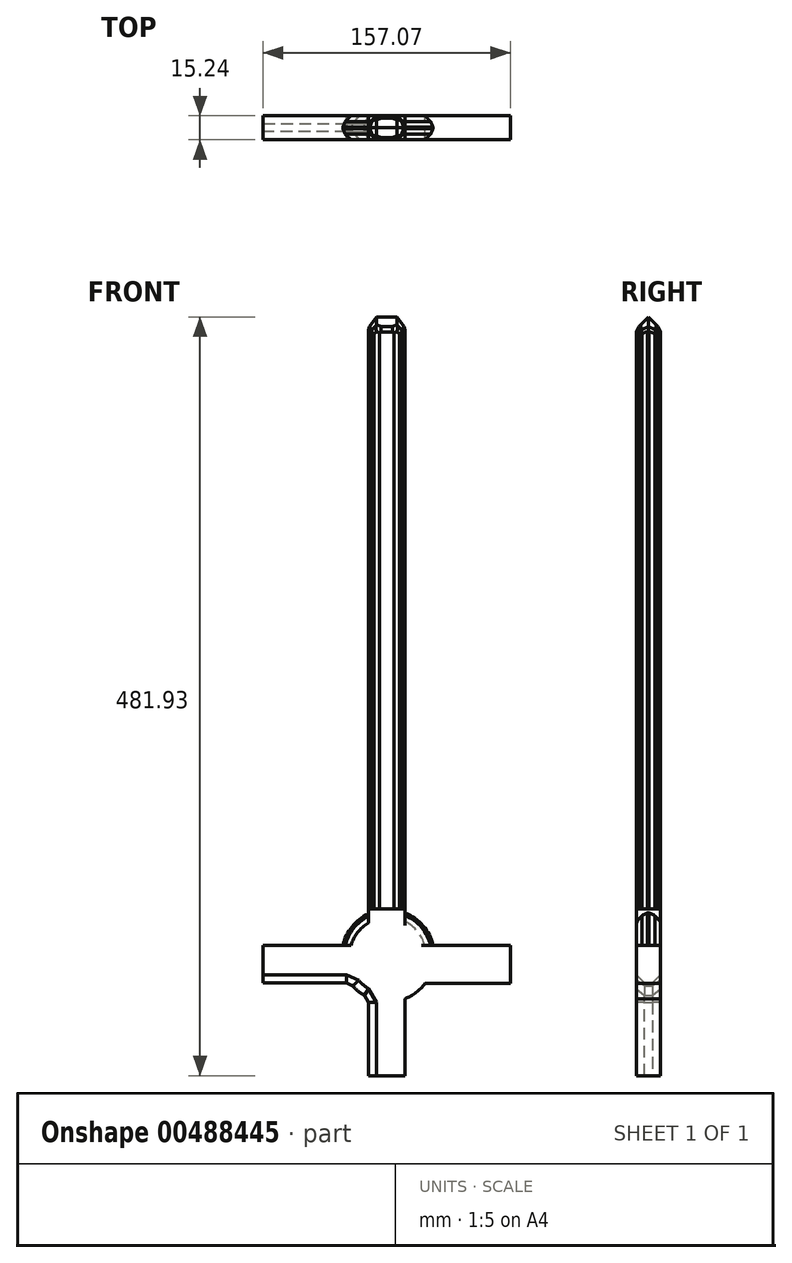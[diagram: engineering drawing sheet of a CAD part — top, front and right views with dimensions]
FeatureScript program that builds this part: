
annotation { "Feature Type Name" : "Feature", "Feature Type Description" : "" }
export const myFeature = defineFeature(function(context is Context, id is Id, definition is map)
    precondition{}
    {
        {
            var Q0;
            Q0=qCreatedBy(makeId("Front.planeOp"),FACE);
            var sketch = newSketch(context, id + "F0", { "sketchPlane" : qUnion([Q0])});
            skLineSegment(sketch, "E0.bottom", {"start": v(10.92, 47.62) * mm, "end": v(-12.46, 47.62) * mm});
            skLineSegment(sketch, "E0.top", {"start": v(10.92, 24.24) * mm, "end": v(-12.46, 24.24) * mm});
            skLineSegment(sketch, "E0.left", {"start": v(10.92, 47.62) * mm, "end": v(10.92, 24.24) * mm});
            skLineSegment(sketch, "E0.right", {"start": v(-12.46, 47.62) * mm, "end": v(-12.46, 24.24) * mm});
            skLineSegment(sketch, "E1.bottom", {"start": v(-12.46, 24.24) * mm, "end": v(-41.2, 24.24) * mm});
            skLineSegment(sketch, "E1.top", {"start": v(-12.46, 0.48) * mm, "end": v(-41.2, 0.48) * mm});
            skLineSegment(sketch, "E1.left", {"start": v(-12.46, 24.24) * mm, "end": v(-12.46, 0.48) * mm});
            skLineSegment(sketch, "E1.right", {"start": v(-41.2, 24.24) * mm, "end": v(-41.2, 0.48) * mm});
            skLineSegment(sketch, "E2.bottom", {"start": v(-12.46, 24.24) * mm, "end": v(10.92, 24.24) * mm});
            skLineSegment(sketch, "E2.top", {"start": v(-12.46, 0.29) * mm, "end": v(10.92, 0.29) * mm});
            skLineSegment(sketch, "E2.left", {"start": v(-12.46, 24.24) * mm, "end": v(-12.46, 0.29) * mm});
            skLineSegment(sketch, "E2.right", {"start": v(10.92, 24.24) * mm, "end": v(10.92, 0.29) * mm});
            skLineSegment(sketch, "E3.bottom", {"start": v(10.92, 24.24) * mm, "end": v(39.67, 24.24) * mm});
            skLineSegment(sketch, "E3.top", {"start": v(10.92, 0.1) * mm, "end": v(39.67, 0.1) * mm});
            skLineSegment(sketch, "E3.left", {"start": v(10.92, 24.24) * mm, "end": v(10.92, 0.1) * mm});
            skLineSegment(sketch, "E3.right", {"start": v(39.67, 24.24) * mm, "end": v(39.67, 0.1) * mm});
            skSolve(sketch);
        }
        {
            var Q0;
            Q0 = qSketchRegion(id + "F0", true);
            extrude(context, id + "F1", {"entities" : qUnion([Q0]), "depth" : 15.24 * mm});
        }
        {
            var Q0;
            Q0=makeQuery(id+"F1.opExtrude","SWEPT_FACE",FACE,{"disambiguationData":[OSD([sQuery(id+"F0.wireOp",EDGE,"E2.top")])]});
            extrude(context, id + "F2", {"entities" : qUnion([Q0]), "operationType" : NewBodyOperationType.ADD, "depth" : 58.67 * mm});
        }
        {
            var Q0;
            Q0=makeQuery(id+"F1.opExtrude","SWEPT_FACE",FACE,{"disambiguationData":[OSD([sQuery(id+"F0.wireOp",EDGE,"E0.bottom")])]});
            extrude(context, id + "F3", {"entities" : qUnion([Q0]), "depth" : 381 * mm});
        }
        {
            var Q0;
            Q0=makeQuery(id+"F1.opExtrude","SWEPT_FACE",FACE,{"disambiguationData":[OSD([sQuery(id+"F0.wireOp",EDGE,"E1.right")])]});
            extrude(context, id + "F4", {"entities" : qUnion([Q0]), "operationType" : NewBodyOperationType.ADD, "depth" : 38.1 * mm});
        }
        {
            var Q0;
            Q0=makeQuery(id+"F1.opExtrude","SWEPT_FACE",FACE,{"disambiguationData":[OSD([sQuery(id+"F0.wireOp",EDGE,"E3.right")])]});
            extrude(context, id + "F5", {"entities" : qUnion([Q0]), "operationType" : NewBodyOperationType.ADD, "depth" : 38.1 * mm});
        }
        {
            var Q0;
            {var subQ0=sQuery(id+"F0.wireOp",EDGE,"E0.bottom");Q0=makeQuery(id+"F3.opExtrude","CAP_EDGE",EDGE,{"disambiguationData":[OSD([subQ0]),TDD([makeQuery(id+"F1.opExtrude","CAP_EDGE",EDGE,{"disambiguationData":[OSD([subQ0])],"isStart":true})])],"isStart":false});}
            var Q1;
            {var subQ0=sQuery(id+"F0.wireOp",EDGE,"E0.bottom");Q1=makeQuery(id+"F3.opExtrude","CAP_EDGE",EDGE,{"disambiguationData":[OSD([subQ0]),TDD([makeQuery(id+"F1.opExtrude","CAP_EDGE",EDGE,{"disambiguationData":[OSD([subQ0])],"isStart":false})])],"isStart":false});}
            chamfer(context, id + "F6", {"entities" : qUnion([Q0, Q1]), "width" : 12.7 * mm, "tangentPropagation" : true});
        }
        {
            var Q0;
            {var subQ0=sQuery(id+"F0.wireOp",EDGE,"E0.bottom");Q0=makeQuery(id+"F6.opChamfer","BLEND_EDGE",EDGE,{"blendedFrom":[makeQuery(id+"F3.opExtrude","CAP_EDGE",EDGE,{"disambiguationData":[OSD([subQ0]),TDD([makeQuery(id+"F1.opExtrude","CAP_EDGE",EDGE,{"disambiguationData":[OSD([subQ0])],"isStart":true})])],"isStart":false}),makeQuery(id+"F3.opExtrude","SWEPT_FACE",FACE,{"disambiguationData":[OSD([subQ0,sQuery(id+"F0.wireOp",EDGE,"E0.left")])]})],"blendedInto":[makeQuery(id+"F3.opExtrude","SWEPT_FACE",FACE,{"disambiguationData":[OSD([subQ0,sQuery(id+"F0.wireOp",EDGE,"E0.left")])]})]});}
            var Q1;
            {var subQ0=sQuery(id+"F0.wireOp",EDGE,"E0.bottom");Q1=makeQuery(id+"F6.opChamfer","BLEND_EDGE",EDGE,{"blendedFrom":[makeQuery(id+"F3.opExtrude","CAP_EDGE",EDGE,{"disambiguationData":[OSD([subQ0]),TDD([makeQuery(id+"F1.opExtrude","CAP_EDGE",EDGE,{"disambiguationData":[OSD([subQ0])],"isStart":false})])],"isStart":false}),makeQuery(id+"F3.opExtrude","SWEPT_FACE",FACE,{"disambiguationData":[OSD([subQ0,sQuery(id+"F0.wireOp",EDGE,"E0.left")])]})],"blendedInto":[makeQuery(id+"F3.opExtrude","SWEPT_FACE",FACE,{"disambiguationData":[OSD([subQ0,sQuery(id+"F0.wireOp",EDGE,"E0.left")])]})]});}
            var Q2;
            {var subQ0=sQuery(id+"F0.wireOp",EDGE,"E0.bottom");Q2=makeQuery(id+"F6.opChamfer","BLEND_EDGE",EDGE,{"blendedFrom":[makeQuery(id+"F3.opExtrude","CAP_EDGE",EDGE,{"disambiguationData":[OSD([subQ0]),TDD([makeQuery(id+"F1.opExtrude","CAP_EDGE",EDGE,{"disambiguationData":[OSD([subQ0])],"isStart":false})])],"isStart":false}),makeQuery(id+"F3.opExtrude","SWEPT_FACE",FACE,{"disambiguationData":[OSD([subQ0,sQuery(id+"F0.wireOp",EDGE,"E0.right")])]})],"blendedInto":[makeQuery(id+"F3.opExtrude","SWEPT_FACE",FACE,{"disambiguationData":[OSD([subQ0,sQuery(id+"F0.wireOp",EDGE,"E0.right")])]})]});}
            var Q3;
            {var subQ0=sQuery(id+"F0.wireOp",EDGE,"E0.bottom");Q3=makeQuery(id+"F6.opChamfer","BLEND_EDGE",EDGE,{"blendedFrom":[makeQuery(id+"F3.opExtrude","CAP_EDGE",EDGE,{"disambiguationData":[OSD([subQ0]),TDD([makeQuery(id+"F1.opExtrude","CAP_EDGE",EDGE,{"disambiguationData":[OSD([subQ0])],"isStart":true})])],"isStart":false}),makeQuery(id+"F3.opExtrude","SWEPT_FACE",FACE,{"disambiguationData":[OSD([subQ0,sQuery(id+"F0.wireOp",EDGE,"E0.right")])]})],"blendedInto":[makeQuery(id+"F3.opExtrude","SWEPT_FACE",FACE,{"disambiguationData":[OSD([subQ0,sQuery(id+"F0.wireOp",EDGE,"E0.right")])]})]});}
            chamfer(context, id + "F7", {"entities" : qUnion([Q0, Q1, Q2, Q3]), "width" : 5.08 * mm, "tangentPropagation" : true});
        }
        {
            var Q0;
            {var subQ0=sQuery(id+"F0.wireOp",EDGE,"E0.right");var subQ1=sQuery(id+"F0.wireOp",EDGE,"E0.bottom");Q0=makeQuery(id+"F3.opExtrude","SWEPT_EDGE",EDGE,{"disambiguationData":[OSD([subQ1,subQ0]),TDD([makeQuery(id+"F1.opExtrude","CAP_VERTEX",VERTEX,{"disambiguationData":[OSD([subQ1,subQ0])],"isStart":false})])]});}
            var Q1;
            {var subQ0=sQuery(id+"F0.wireOp",EDGE,"E0.left");var subQ1=sQuery(id+"F0.wireOp",EDGE,"E0.bottom");Q1=makeQuery(id+"F3.opExtrude","SWEPT_EDGE",EDGE,{"disambiguationData":[OSD([subQ1,subQ0]),TDD([makeQuery(id+"F1.opExtrude","CAP_VERTEX",VERTEX,{"disambiguationData":[OSD([subQ1,subQ0])],"isStart":false})])]});}
            var Q2;
            {var subQ0=sQuery(id+"F0.wireOp",EDGE,"E0.left");var subQ1=sQuery(id+"F0.wireOp",EDGE,"E0.bottom");Q2=makeQuery(id+"F3.opExtrude","SWEPT_EDGE",EDGE,{"disambiguationData":[OSD([subQ1,subQ0]),TDD([makeQuery(id+"F1.opExtrude","CAP_VERTEX",VERTEX,{"disambiguationData":[OSD([subQ1,subQ0])],"isStart":true})])]});}
            var Q3;
            {var subQ0=sQuery(id+"F0.wireOp",EDGE,"E0.right");var subQ1=sQuery(id+"F0.wireOp",EDGE,"E0.bottom");Q3=makeQuery(id+"F3.opExtrude","SWEPT_EDGE",EDGE,{"disambiguationData":[OSD([subQ1,subQ0]),TDD([makeQuery(id+"F1.opExtrude","CAP_VERTEX",VERTEX,{"disambiguationData":[OSD([subQ1,subQ0])],"isStart":true})])]});}
            chamfer(context, id + "F8", {"entities" : qUnion([Q0, Q1, Q2, Q3]), "width" : 5.08 * mm, "tangentPropagation" : true});
        }
        {
            var Q0;
            Q0=qCreatedBy(makeId("Front.planeOp"),FACE);
            var sketch = newSketch(context, id + "F9", { "sketchPlane" : qUnion([Q0])});
            skCircle(sketch, "E4", {"center": v(0, 17.76) * mm, "radius": 29.39 * mm});
            skSolve(sketch);
        }
        {
            var Q0;
            Q0 = qSketchRegion(id + "F9", true);
            extrude(context, id + "F10", {"entities" : qUnion([Q0]), "operationType" : NewBodyOperationType.ADD, "depth" : 15.24 * mm});
        }
        {
            var Q0;
            {var subQ4=sQuery(id+"F0.wireOp",EDGE,"E0.right");var subQ5=sQuery(id+"F9.wireOp",EDGE,"E4");Q0=makeQuery(id+"F10.boolean.opBoolean","SPLIT",EDGE,{"disambiguationData":[TD([makeQuery(id+"F1.opExtrude","SWEPT_FACE",FACE,{"disambiguationData":[OSD([subQ4])]})])],"derivedFrom":makeQuery(id+"F10.opExtrude","CAP_EDGE",EDGE,{"disambiguationData":[OSD([subQ5])],"isStart":false})});}
            var Q1;
            {var subQ3=sQuery(id+"F0.wireOp",EDGE,"E0.right");var subQ5=sQuery(id+"F9.wireOp",EDGE,"E4");Q1=makeQuery(id+"F10.boolean.opBoolean","SPLIT",EDGE,{"disambiguationData":[TD([makeQuery(id+"F1.opExtrude","SWEPT_FACE",FACE,{"disambiguationData":[OSD([subQ3])]})])],"derivedFrom":makeQuery(id+"F10.opExtrude","CAP_EDGE",EDGE,{"disambiguationData":[OSD([subQ5])],"isStart":true})});}
            var Q2;
            {var subQ2=sQuery(id+"F0.wireOp",EDGE,"E0.left");var subQ5=sQuery(id+"F9.wireOp",EDGE,"E4");Q2=makeQuery(id+"F10.boolean.opBoolean","SPLIT",EDGE,{"disambiguationData":[TD([makeQuery(id+"F1.opExtrude","SWEPT_FACE",FACE,{"disambiguationData":[OSD([subQ2])]})])],"derivedFrom":makeQuery(id+"F10.opExtrude","CAP_EDGE",EDGE,{"disambiguationData":[OSD([subQ5])],"isStart":true})});}
            var Q3;
            {var subQ2=sQuery(id+"F9.wireOp",EDGE,"E4");var subQ3=sQuery(id+"F0.wireOp",EDGE,"E0.left");Q3=makeQuery(id+"F10.boolean.opBoolean","SPLIT",EDGE,{"disambiguationData":[TD([makeQuery(id+"F1.opExtrude","SWEPT_FACE",FACE,{"disambiguationData":[OSD([subQ3])]})])],"derivedFrom":makeQuery(id+"F10.opExtrude","CAP_EDGE",EDGE,{"disambiguationData":[OSD([subQ2])],"isStart":false})});}
            chamfer(context, id + "F11", {"entities" : qUnion([Q0, Q1, Q2, Q3]), "width" : 5.08 * mm, "tangentPropagation" : true});
        }
        {
            var Q0;
            {var subQ12=sQuery(id+"F0.wireOp",EDGE,"E0.right");var subQ16=makeQuery(id+"F1.opExtrude","SWEPT_FACE",FACE,{"disambiguationData":[OSD([subQ12])]});var subQ17=sQuery(id+"F9.wireOp",EDGE,"E4");var subQ21=makeQuery(id+"F10.opExtrude","SWEPT_FACE",FACE,{"disambiguationData":[OSD([subQ17])]});Q0=makeQuery(id+"F11.opChamfer","BLEND_EDGE",EDGE,{"blendedFrom":[makeQuery(id+"F10.boolean.opBoolean","SPLIT",EDGE,{"disambiguationData":[TD([subQ16])],"derivedFrom":makeQuery(id+"F10.opExtrude","CAP_EDGE",EDGE,{"disambiguationData":[OSD([subQ17])],"isStart":false})}),makeQuery(id+"F10.boolean.opBoolean","SPLIT",FACE,{"disambiguationData":[TD([subQ16])],"derivedFrom":subQ21})],"blendedInto":[makeQuery(id+"F10.boolean.opBoolean","SPLIT",FACE,{"disambiguationData":[TD([subQ16])],"derivedFrom":subQ21})]});}
            var Q1;
            {var subQ11=sQuery(id+"F0.wireOp",EDGE,"E0.right");var subQ16=makeQuery(id+"F1.opExtrude","SWEPT_FACE",FACE,{"disambiguationData":[OSD([subQ11])]});var subQ17=sQuery(id+"F9.wireOp",EDGE,"E4");var subQ21=makeQuery(id+"F10.opExtrude","SWEPT_FACE",FACE,{"disambiguationData":[OSD([subQ17])]});Q1=makeQuery(id+"F11.opChamfer","BLEND_EDGE",EDGE,{"blendedFrom":[makeQuery(id+"F10.boolean.opBoolean","SPLIT",EDGE,{"disambiguationData":[TD([subQ16])],"derivedFrom":makeQuery(id+"F10.opExtrude","CAP_EDGE",EDGE,{"disambiguationData":[OSD([subQ17])],"isStart":true})}),makeQuery(id+"F10.boolean.opBoolean","SPLIT",FACE,{"disambiguationData":[TD([subQ16])],"derivedFrom":subQ21})],"blendedInto":[makeQuery(id+"F10.boolean.opBoolean","SPLIT",FACE,{"disambiguationData":[TD([subQ16])],"derivedFrom":subQ21})]});}
            var Q2;
            {var subQ14=sQuery(id+"F0.wireOp",EDGE,"E0.left");var subQ18=makeQuery(id+"F1.opExtrude","SWEPT_FACE",FACE,{"disambiguationData":[OSD([subQ14])]});var subQ19=sQuery(id+"F9.wireOp",EDGE,"E4");var subQ21=makeQuery(id+"F10.opExtrude","SWEPT_FACE",FACE,{"disambiguationData":[OSD([subQ19])]});Q2=makeQuery(id+"F11.opChamfer","BLEND_EDGE",EDGE,{"blendedFrom":[makeQuery(id+"F10.boolean.opBoolean","SPLIT",EDGE,{"disambiguationData":[TD([subQ18])],"derivedFrom":makeQuery(id+"F10.opExtrude","CAP_EDGE",EDGE,{"disambiguationData":[OSD([subQ19])],"isStart":false})}),makeQuery(id+"F10.boolean.opBoolean","SPLIT",FACE,{"disambiguationData":[TD([subQ18])],"derivedFrom":subQ21})],"blendedInto":[makeQuery(id+"F10.boolean.opBoolean","SPLIT",FACE,{"disambiguationData":[TD([subQ18])],"derivedFrom":subQ21})]});}
            var Q3;
            {var subQ14=sQuery(id+"F0.wireOp",EDGE,"E0.left");var subQ18=makeQuery(id+"F1.opExtrude","SWEPT_FACE",FACE,{"disambiguationData":[OSD([subQ14])]});var subQ19=sQuery(id+"F9.wireOp",EDGE,"E4");var subQ21=makeQuery(id+"F10.opExtrude","SWEPT_FACE",FACE,{"disambiguationData":[OSD([subQ19])]});Q3=makeQuery(id+"F11.opChamfer","BLEND_EDGE",EDGE,{"blendedFrom":[makeQuery(id+"F10.boolean.opBoolean","SPLIT",EDGE,{"disambiguationData":[TD([subQ18])],"derivedFrom":makeQuery(id+"F10.opExtrude","CAP_EDGE",EDGE,{"disambiguationData":[OSD([subQ19])],"isStart":true})}),makeQuery(id+"F10.boolean.opBoolean","SPLIT",FACE,{"disambiguationData":[TD([subQ18])],"derivedFrom":subQ21})],"blendedInto":[makeQuery(id+"F10.boolean.opBoolean","SPLIT",FACE,{"disambiguationData":[TD([subQ18])],"derivedFrom":subQ21})]});}
            chamfer(context, id + "F12", {"entities" : qUnion([Q0, Q1, Q2, Q3]), "width" : 5.08 * mm, "tangentPropagation" : true});
        }
        {
            var Q0;
            {var subQ0=sQuery(id+"F9.wireOp",EDGE,"E4");var subQ1=makeQuery(id+"F10.opExtrude","CAP_FACE",FACE,{"disambiguationData":[OSD([subQ0])],"isStart":false});var subQ2=sQuery(id+"F0.wireOp",EDGE,"E3.right");var subQ3=makeQuery(id+"F5.opExtrude","SWEPT_FACE",FACE,{"disambiguationData":[OSD([subQ2]),TDD([makeQuery(id+"F1.opExtrude","CAP_EDGE",EDGE,{"disambiguationData":[OSD([subQ2])],"isStart":false})])]});var subQ4=sQuery(id+"F0.wireOp",EDGE,"E1.right");var subQ5=makeQuery(id+"F4.opExtrude","SWEPT_FACE",FACE,{"disambiguationData":[OSD([subQ4]),TDD([makeQuery(id+"F1.opExtrude","CAP_EDGE",EDGE,{"disambiguationData":[OSD([subQ4])],"isStart":false})])]});var subQ6=sQuery(id+"F0.wireOp",EDGE,"E2.top");var subQ7=makeQuery(id+"F2.opExtrude","SWEPT_FACE",FACE,{"disambiguationData":[OSD([subQ6]),TDD([makeQuery(id+"F1.opExtrude","CAP_EDGE",EDGE,{"disambiguationData":[OSD([subQ6])],"isStart":false})])]});var subQ8=sQuery(id+"F0.wireOp",EDGE,"E3.bottom");var subQ9=sQuery(id+"F0.wireOp",EDGE,"E0.left");var subQ10=makeQuery(id+"F1.opExtrude","CAP_FACE",FACE,{"disambiguationData":[OSD([sQuery(id+"F0.wireOp",EDGE,"E0.bottom"),subQ9,sQuery(id+"F0.wireOp",EDGE,"E0.right"),sQuery(id+"F0.wireOp",EDGE,"E1.bottom"),sQuery(id+"F0.wireOp",EDGE,"E1.top"),subQ4,subQ6,sQuery(id+"F0.wireOp",EDGE,"E2.left"),subQ8,sQuery(id+"F0.wireOp",EDGE,"E3.top"),sQuery(id+"F0.wireOp",EDGE,"E3.left"),subQ2])],"isStart":false});Q0=makeQuery(id+"F11.opChamfer","BLEND_EDGE",EDGE,{"blendedFrom":[makeQuery(id+"F10.boolean.opBoolean","SPLIT",EDGE,{"disambiguationData":[TD([makeQuery(id+"F1.opExtrude","SWEPT_FACE",FACE,{"disambiguationData":[OSD([subQ9])]})])],"derivedFrom":makeQuery(id+"F10.opExtrude","CAP_EDGE",EDGE,{"disambiguationData":[OSD([subQ0])],"isStart":false})}),makeQuery(id+"F10.boolean.opBoolean","MERGE",FACE,{"derivedFrom":[makeQuery(id+"F5.boolean.opBoolean","MERGE",FACE,{"derivedFrom":[makeQuery(id+"F4.boolean.opBoolean","MERGE",FACE,{"derivedFrom":[makeQuery(id+"F2.boolean.opBoolean","MERGE",FACE,{"derivedFrom":[subQ10,subQ7]}),subQ5]}),subQ3]}),subQ1]})],"blendedInto":[makeQuery(id+"F10.boolean.opBoolean","MERGE",FACE,{"derivedFrom":[makeQuery(id+"F5.boolean.opBoolean","MERGE",FACE,{"derivedFrom":[makeQuery(id+"F4.boolean.opBoolean","MERGE",FACE,{"derivedFrom":[makeQuery(id+"F2.boolean.opBoolean","MERGE",FACE,{"derivedFrom":[subQ10,subQ7]}),subQ5]}),subQ3]}),subQ1]})]});}
            fillet(context, id + "F13", {"entities" : qUnion([Q0]), "radius" : 5.08 * mm, "tangentPropagation" : true, "allowEdgeOverflow" : false});
        }
        {
            var Q0;
            {var subQ0=sQuery(id+"F0.wireOp",EDGE,"E0.right");var subQ1=sQuery(id+"F0.wireOp",EDGE,"E0.bottom");Q0=makeQuery(id+"F8.opChamfer","BLEND_EDGE",EDGE,{"blendedFrom":[makeQuery(id+"F3.opExtrude","SWEPT_EDGE",EDGE,{"disambiguationData":[OSD([subQ1,subQ0]),TDD([makeQuery(id+"F1.opExtrude","CAP_VERTEX",VERTEX,{"disambiguationData":[OSD([subQ1,subQ0])],"isStart":true})])]}),makeQuery(id+"F3.opExtrude","SWEPT_FACE",FACE,{"disambiguationData":[OSD([subQ1,subQ0])]})],"blendedInto":[makeQuery(id+"F3.opExtrude","SWEPT_FACE",FACE,{"disambiguationData":[OSD([subQ1,subQ0])]})]});}
            var Q1;
            {var subQ0=sQuery(id+"F0.wireOp",EDGE,"E0.right");var subQ1=sQuery(id+"F0.wireOp",EDGE,"E0.bottom");Q1=makeQuery(id+"F8.opChamfer","BLEND_EDGE",EDGE,{"blendedFrom":[makeQuery(id+"F3.opExtrude","SWEPT_EDGE",EDGE,{"disambiguationData":[OSD([subQ1,subQ0]),TDD([makeQuery(id+"F1.opExtrude","CAP_VERTEX",VERTEX,{"disambiguationData":[OSD([subQ1,subQ0])],"isStart":false})])]}),makeQuery(id+"F3.opExtrude","SWEPT_FACE",FACE,{"disambiguationData":[OSD([subQ1,subQ0])]})],"blendedInto":[makeQuery(id+"F3.opExtrude","SWEPT_FACE",FACE,{"disambiguationData":[OSD([subQ1,subQ0])]})]});}
            var Q2;
            {var subQ0=sQuery(id+"F0.wireOp",EDGE,"E0.left");var subQ1=sQuery(id+"F0.wireOp",EDGE,"E0.bottom");Q2=makeQuery(id+"F8.opChamfer","BLEND_EDGE",EDGE,{"blendedFrom":[makeQuery(id+"F3.opExtrude","SWEPT_EDGE",EDGE,{"disambiguationData":[OSD([subQ1,subQ0]),TDD([makeQuery(id+"F1.opExtrude","CAP_VERTEX",VERTEX,{"disambiguationData":[OSD([subQ1,subQ0])],"isStart":true})])]}),makeQuery(id+"F3.opExtrude","SWEPT_FACE",FACE,{"disambiguationData":[OSD([subQ1,subQ0])]})],"blendedInto":[makeQuery(id+"F3.opExtrude","SWEPT_FACE",FACE,{"disambiguationData":[OSD([subQ1,subQ0])]})]});}
            var Q3;
            {var subQ0=sQuery(id+"F0.wireOp",EDGE,"E0.left");var subQ1=sQuery(id+"F0.wireOp",EDGE,"E0.bottom");Q3=makeQuery(id+"F8.opChamfer","BLEND_EDGE",EDGE,{"blendedFrom":[makeQuery(id+"F3.opExtrude","SWEPT_EDGE",EDGE,{"disambiguationData":[OSD([subQ1,subQ0]),TDD([makeQuery(id+"F1.opExtrude","CAP_VERTEX",VERTEX,{"disambiguationData":[OSD([subQ1,subQ0])],"isStart":false})])]}),makeQuery(id+"F3.opExtrude","SWEPT_FACE",FACE,{"disambiguationData":[OSD([subQ1,subQ0])]})],"blendedInto":[makeQuery(id+"F3.opExtrude","SWEPT_FACE",FACE,{"disambiguationData":[OSD([subQ1,subQ0])]})]});}
            chamfer(context, id + "F14", {"entities" : qUnion([Q0, Q1, Q2, Q3]), "width" : 5.08 * mm, "tangentPropagation" : true});
        }
        {
            var Q0;
            {var subQ0=sQuery(id+"F0.wireOp",EDGE,"E0.bottom");var subQ1=sQuery(id+"F0.wireOp",EDGE,"E0.left");Q0=makeQuery(id+"F8.opChamfer","BLEND_EDGE",EDGE,{"blendedFrom":[makeQuery(id+"F3.opExtrude","SWEPT_EDGE",EDGE,{"disambiguationData":[OSD([subQ0,subQ1]),TDD([makeQuery(id+"F1.opExtrude","CAP_VERTEX",VERTEX,{"disambiguationData":[OSD([subQ0,subQ1])],"isStart":true})])]}),makeQuery(id+"F3.opExtrude","SWEPT_FACE",FACE,{"disambiguationData":[OSD([subQ0]),TDD([makeQuery(id+"F1.opExtrude","CAP_EDGE",EDGE,{"disambiguationData":[OSD([subQ0])],"isStart":true})])]})],"blendedInto":[makeQuery(id+"F3.opExtrude","SWEPT_FACE",FACE,{"disambiguationData":[OSD([subQ0]),TDD([makeQuery(id+"F1.opExtrude","CAP_EDGE",EDGE,{"disambiguationData":[OSD([subQ0])],"isStart":true})])]})]});}
            var Q1;
            {var subQ0=sQuery(id+"F0.wireOp",EDGE,"E0.bottom");var subQ1=sQuery(id+"F0.wireOp",EDGE,"E0.right");Q1=makeQuery(id+"F8.opChamfer","BLEND_EDGE",EDGE,{"blendedFrom":[makeQuery(id+"F3.opExtrude","SWEPT_EDGE",EDGE,{"disambiguationData":[OSD([subQ0,subQ1]),TDD([makeQuery(id+"F1.opExtrude","CAP_VERTEX",VERTEX,{"disambiguationData":[OSD([subQ0,subQ1])],"isStart":true})])]}),makeQuery(id+"F3.opExtrude","SWEPT_FACE",FACE,{"disambiguationData":[OSD([subQ0]),TDD([makeQuery(id+"F1.opExtrude","CAP_EDGE",EDGE,{"disambiguationData":[OSD([subQ0])],"isStart":true})])]})],"blendedInto":[makeQuery(id+"F3.opExtrude","SWEPT_FACE",FACE,{"disambiguationData":[OSD([subQ0]),TDD([makeQuery(id+"F1.opExtrude","CAP_EDGE",EDGE,{"disambiguationData":[OSD([subQ0])],"isStart":true})])]})]});}
            var Q2;
            {var subQ0=sQuery(id+"F0.wireOp",EDGE,"E0.bottom");var subQ1=sQuery(id+"F0.wireOp",EDGE,"E0.right");Q2=makeQuery(id+"F8.opChamfer","BLEND_EDGE",EDGE,{"blendedFrom":[makeQuery(id+"F3.opExtrude","SWEPT_EDGE",EDGE,{"disambiguationData":[OSD([subQ0,subQ1]),TDD([makeQuery(id+"F1.opExtrude","CAP_VERTEX",VERTEX,{"disambiguationData":[OSD([subQ0,subQ1])],"isStart":false})])]}),makeQuery(id+"F3.opExtrude","SWEPT_FACE",FACE,{"disambiguationData":[OSD([subQ0]),TDD([makeQuery(id+"F1.opExtrude","CAP_EDGE",EDGE,{"disambiguationData":[OSD([subQ0])],"isStart":false})])]})],"blendedInto":[makeQuery(id+"F3.opExtrude","SWEPT_FACE",FACE,{"disambiguationData":[OSD([subQ0]),TDD([makeQuery(id+"F1.opExtrude","CAP_EDGE",EDGE,{"disambiguationData":[OSD([subQ0])],"isStart":false})])]})]});}
            var Q3;
            {var subQ0=sQuery(id+"F0.wireOp",EDGE,"E0.bottom");var subQ1=sQuery(id+"F0.wireOp",EDGE,"E0.left");Q3=makeQuery(id+"F8.opChamfer","BLEND_EDGE",EDGE,{"blendedFrom":[makeQuery(id+"F3.opExtrude","SWEPT_EDGE",EDGE,{"disambiguationData":[OSD([subQ0,subQ1]),TDD([makeQuery(id+"F1.opExtrude","CAP_VERTEX",VERTEX,{"disambiguationData":[OSD([subQ0,subQ1])],"isStart":false})])]}),makeQuery(id+"F3.opExtrude","SWEPT_FACE",FACE,{"disambiguationData":[OSD([subQ0]),TDD([makeQuery(id+"F1.opExtrude","CAP_EDGE",EDGE,{"disambiguationData":[OSD([subQ0])],"isStart":false})])]})],"blendedInto":[makeQuery(id+"F3.opExtrude","SWEPT_FACE",FACE,{"disambiguationData":[OSD([subQ0]),TDD([makeQuery(id+"F1.opExtrude","CAP_EDGE",EDGE,{"disambiguationData":[OSD([subQ0])],"isStart":false})])]})]});}
            chamfer(context, id + "F15", {"entities" : qUnion([Q0, Q1, Q2, Q3]), "width" : 5.08 * mm, "tangentPropagation" : true});
        }
        {
            var Q0;
            {var subQ0=sQuery(id+"F0.wireOp",EDGE,"E0.left");var subQ1=sQuery(id+"F0.wireOp",EDGE,"E0.bottom");var subQ2=makeQuery(id+"F1.opExtrude","CAP_EDGE",EDGE,{"disambiguationData":[OSD([subQ1])],"isStart":true});Q0=makeQuery(id+"F15.opChamfer","BLEND_EDGE",EDGE,{"blendedFrom":[makeQuery(id+"F8.opChamfer","BLEND_EDGE",EDGE,{"blendedFrom":[makeQuery(id+"F3.opExtrude","SWEPT_EDGE",EDGE,{"disambiguationData":[OSD([subQ1,subQ0]),TDD([makeQuery(id+"F1.opExtrude","CAP_VERTEX",VERTEX,{"disambiguationData":[OSD([subQ1,subQ0])],"isStart":true})])]}),makeQuery(id+"F3.opExtrude","SWEPT_FACE",FACE,{"disambiguationData":[OSD([subQ1]),TDD([subQ2])]})],"blendedInto":[makeQuery(id+"F3.opExtrude","SWEPT_FACE",FACE,{"disambiguationData":[OSD([subQ1]),TDD([subQ2])]})]}),makeQuery(id+"F7.opChamfer","BLEND_FACE",FACE,{"disambiguationData":[OSD([subQ1,subQ0]),TDD([makeQuery(id+"F6.opChamfer","BLEND_EDGE",EDGE,{"blendedFrom":[makeQuery(id+"F3.opExtrude","CAP_EDGE",EDGE,{"disambiguationData":[OSD([subQ1]),TDD([subQ2])],"isStart":false}),makeQuery(id+"F3.opExtrude","SWEPT_FACE",FACE,{"disambiguationData":[OSD([subQ1,subQ0])]})],"blendedInto":[makeQuery(id+"F3.opExtrude","SWEPT_FACE",FACE,{"disambiguationData":[OSD([subQ1,subQ0])]})]})])]})],"blendedInto":[makeQuery(id+"F7.opChamfer","BLEND_FACE",FACE,{"disambiguationData":[OSD([subQ1,subQ0]),TDD([makeQuery(id+"F6.opChamfer","BLEND_EDGE",EDGE,{"blendedFrom":[makeQuery(id+"F3.opExtrude","CAP_EDGE",EDGE,{"disambiguationData":[OSD([subQ1]),TDD([subQ2])],"isStart":false}),makeQuery(id+"F3.opExtrude","SWEPT_FACE",FACE,{"disambiguationData":[OSD([subQ1,subQ0])]})],"blendedInto":[makeQuery(id+"F3.opExtrude","SWEPT_FACE",FACE,{"disambiguationData":[OSD([subQ1,subQ0])]})]})])]})]});}
            var Q1;
            {var subQ0=sQuery(id+"F0.wireOp",EDGE,"E0.bottom");var subQ1=makeQuery(id+"F1.opExtrude","CAP_EDGE",EDGE,{"disambiguationData":[OSD([subQ0])],"isStart":true});var subQ2=sQuery(id+"F0.wireOp",EDGE,"E0.left");Q1=makeQuery(id+"F15.opChamfer","BLEND_EDGE",EDGE,{"blendedFrom":[makeQuery(id+"F8.opChamfer","BLEND_EDGE",EDGE,{"blendedFrom":[makeQuery(id+"F3.opExtrude","SWEPT_EDGE",EDGE,{"disambiguationData":[OSD([subQ0,subQ2]),TDD([makeQuery(id+"F1.opExtrude","CAP_VERTEX",VERTEX,{"disambiguationData":[OSD([subQ0,subQ2])],"isStart":true})])]}),makeQuery(id+"F3.opExtrude","SWEPT_FACE",FACE,{"disambiguationData":[OSD([subQ0]),TDD([subQ1])]})],"blendedInto":[makeQuery(id+"F3.opExtrude","SWEPT_FACE",FACE,{"disambiguationData":[OSD([subQ0]),TDD([subQ1])]})]}),makeQuery(id+"F6.opChamfer","BLEND_FACE",FACE,{"disambiguationData":[OSD([subQ0]),TDD([makeQuery(id+"F3.opExtrude","CAP_EDGE",EDGE,{"disambiguationData":[OSD([subQ0]),TDD([subQ1])],"isStart":false})])]})],"blendedInto":[makeQuery(id+"F6.opChamfer","BLEND_FACE",FACE,{"disambiguationData":[OSD([subQ0]),TDD([makeQuery(id+"F3.opExtrude","CAP_EDGE",EDGE,{"disambiguationData":[OSD([subQ0]),TDD([subQ1])],"isStart":false})])]})]});}
            var Q2;
            {var subQ0=sQuery(id+"F0.wireOp",EDGE,"E0.bottom");var subQ1=makeQuery(id+"F1.opExtrude","CAP_EDGE",EDGE,{"disambiguationData":[OSD([subQ0])],"isStart":true});Q2=makeQuery(id+"F6.opChamfer","BLEND_EDGE",EDGE,{"blendedFrom":[makeQuery(id+"F3.opExtrude","CAP_EDGE",EDGE,{"disambiguationData":[OSD([subQ0]),TDD([subQ1])],"isStart":false}),makeQuery(id+"F3.opExtrude","SWEPT_FACE",FACE,{"disambiguationData":[OSD([subQ0]),TDD([subQ1])]})],"blendedInto":[makeQuery(id+"F3.opExtrude","SWEPT_FACE",FACE,{"disambiguationData":[OSD([subQ0]),TDD([subQ1])]})]});}
            var Q3;
            {var subQ0=sQuery(id+"F0.wireOp",EDGE,"E0.bottom");var subQ1=makeQuery(id+"F1.opExtrude","CAP_EDGE",EDGE,{"disambiguationData":[OSD([subQ0])],"isStart":true});var subQ2=sQuery(id+"F0.wireOp",EDGE,"E0.right");Q3=makeQuery(id+"F15.opChamfer","BLEND_EDGE",EDGE,{"blendedFrom":[makeQuery(id+"F8.opChamfer","BLEND_EDGE",EDGE,{"blendedFrom":[makeQuery(id+"F3.opExtrude","SWEPT_EDGE",EDGE,{"disambiguationData":[OSD([subQ0,subQ2]),TDD([makeQuery(id+"F1.opExtrude","CAP_VERTEX",VERTEX,{"disambiguationData":[OSD([subQ0,subQ2])],"isStart":true})])]}),makeQuery(id+"F3.opExtrude","SWEPT_FACE",FACE,{"disambiguationData":[OSD([subQ0]),TDD([subQ1])]})],"blendedInto":[makeQuery(id+"F3.opExtrude","SWEPT_FACE",FACE,{"disambiguationData":[OSD([subQ0]),TDD([subQ1])]})]}),makeQuery(id+"F6.opChamfer","BLEND_FACE",FACE,{"disambiguationData":[OSD([subQ0]),TDD([makeQuery(id+"F3.opExtrude","CAP_EDGE",EDGE,{"disambiguationData":[OSD([subQ0]),TDD([subQ1])],"isStart":false})])]})],"blendedInto":[makeQuery(id+"F6.opChamfer","BLEND_FACE",FACE,{"disambiguationData":[OSD([subQ0]),TDD([makeQuery(id+"F3.opExtrude","CAP_EDGE",EDGE,{"disambiguationData":[OSD([subQ0]),TDD([subQ1])],"isStart":false})])]})]});}
            var Q4;
            {var subQ0=sQuery(id+"F0.wireOp",EDGE,"E0.right");var subQ1=sQuery(id+"F0.wireOp",EDGE,"E0.bottom");var subQ2=makeQuery(id+"F1.opExtrude","CAP_EDGE",EDGE,{"disambiguationData":[OSD([subQ1])],"isStart":true});Q4=makeQuery(id+"F15.opChamfer","BLEND_EDGE",EDGE,{"blendedFrom":[makeQuery(id+"F8.opChamfer","BLEND_EDGE",EDGE,{"blendedFrom":[makeQuery(id+"F3.opExtrude","SWEPT_EDGE",EDGE,{"disambiguationData":[OSD([subQ1,subQ0]),TDD([makeQuery(id+"F1.opExtrude","CAP_VERTEX",VERTEX,{"disambiguationData":[OSD([subQ1,subQ0])],"isStart":true})])]}),makeQuery(id+"F3.opExtrude","SWEPT_FACE",FACE,{"disambiguationData":[OSD([subQ1]),TDD([subQ2])]})],"blendedInto":[makeQuery(id+"F3.opExtrude","SWEPT_FACE",FACE,{"disambiguationData":[OSD([subQ1]),TDD([subQ2])]})]}),makeQuery(id+"F7.opChamfer","BLEND_FACE",FACE,{"disambiguationData":[OSD([subQ1,subQ0]),TDD([makeQuery(id+"F6.opChamfer","BLEND_EDGE",EDGE,{"blendedFrom":[makeQuery(id+"F3.opExtrude","CAP_EDGE",EDGE,{"disambiguationData":[OSD([subQ1]),TDD([subQ2])],"isStart":false}),makeQuery(id+"F3.opExtrude","SWEPT_FACE",FACE,{"disambiguationData":[OSD([subQ1,subQ0])]})],"blendedInto":[makeQuery(id+"F3.opExtrude","SWEPT_FACE",FACE,{"disambiguationData":[OSD([subQ1,subQ0])]})]})])]})],"blendedInto":[makeQuery(id+"F7.opChamfer","BLEND_FACE",FACE,{"disambiguationData":[OSD([subQ1,subQ0]),TDD([makeQuery(id+"F6.opChamfer","BLEND_EDGE",EDGE,{"blendedFrom":[makeQuery(id+"F3.opExtrude","CAP_EDGE",EDGE,{"disambiguationData":[OSD([subQ1]),TDD([subQ2])],"isStart":false}),makeQuery(id+"F3.opExtrude","SWEPT_FACE",FACE,{"disambiguationData":[OSD([subQ1,subQ0])]})],"blendedInto":[makeQuery(id+"F3.opExtrude","SWEPT_FACE",FACE,{"disambiguationData":[OSD([subQ1,subQ0])]})]})])]})]});}
            var Q5;
            {var subQ0=sQuery(id+"F0.wireOp",EDGE,"E0.right");var subQ1=sQuery(id+"F0.wireOp",EDGE,"E0.bottom");var subQ2=makeQuery(id+"F1.opExtrude","CAP_EDGE",EDGE,{"disambiguationData":[OSD([subQ1])],"isStart":false});Q5=makeQuery(id+"F15.opChamfer","BLEND_EDGE",EDGE,{"blendedFrom":[makeQuery(id+"F8.opChamfer","BLEND_EDGE",EDGE,{"blendedFrom":[makeQuery(id+"F3.opExtrude","SWEPT_EDGE",EDGE,{"disambiguationData":[OSD([subQ1,subQ0]),TDD([makeQuery(id+"F1.opExtrude","CAP_VERTEX",VERTEX,{"disambiguationData":[OSD([subQ1,subQ0])],"isStart":false})])]}),makeQuery(id+"F3.opExtrude","SWEPT_FACE",FACE,{"disambiguationData":[OSD([subQ1]),TDD([subQ2])]})],"blendedInto":[makeQuery(id+"F3.opExtrude","SWEPT_FACE",FACE,{"disambiguationData":[OSD([subQ1]),TDD([subQ2])]})]}),makeQuery(id+"F7.opChamfer","BLEND_FACE",FACE,{"disambiguationData":[OSD([subQ1,subQ0]),TDD([makeQuery(id+"F6.opChamfer","BLEND_EDGE",EDGE,{"blendedFrom":[makeQuery(id+"F3.opExtrude","CAP_EDGE",EDGE,{"disambiguationData":[OSD([subQ1]),TDD([subQ2])],"isStart":false}),makeQuery(id+"F3.opExtrude","SWEPT_FACE",FACE,{"disambiguationData":[OSD([subQ1,subQ0])]})],"blendedInto":[makeQuery(id+"F3.opExtrude","SWEPT_FACE",FACE,{"disambiguationData":[OSD([subQ1,subQ0])]})]})])]})],"blendedInto":[makeQuery(id+"F7.opChamfer","BLEND_FACE",FACE,{"disambiguationData":[OSD([subQ1,subQ0]),TDD([makeQuery(id+"F6.opChamfer","BLEND_EDGE",EDGE,{"blendedFrom":[makeQuery(id+"F3.opExtrude","CAP_EDGE",EDGE,{"disambiguationData":[OSD([subQ1]),TDD([subQ2])],"isStart":false}),makeQuery(id+"F3.opExtrude","SWEPT_FACE",FACE,{"disambiguationData":[OSD([subQ1,subQ0])]})],"blendedInto":[makeQuery(id+"F3.opExtrude","SWEPT_FACE",FACE,{"disambiguationData":[OSD([subQ1,subQ0])]})]})])]})]});}
            var Q6;
            {var subQ0=sQuery(id+"F0.wireOp",EDGE,"E0.bottom");var subQ1=makeQuery(id+"F1.opExtrude","CAP_EDGE",EDGE,{"disambiguationData":[OSD([subQ0])],"isStart":false});var subQ2=sQuery(id+"F0.wireOp",EDGE,"E0.right");Q6=makeQuery(id+"F15.opChamfer","BLEND_EDGE",EDGE,{"blendedFrom":[makeQuery(id+"F8.opChamfer","BLEND_EDGE",EDGE,{"blendedFrom":[makeQuery(id+"F3.opExtrude","SWEPT_EDGE",EDGE,{"disambiguationData":[OSD([subQ0,subQ2]),TDD([makeQuery(id+"F1.opExtrude","CAP_VERTEX",VERTEX,{"disambiguationData":[OSD([subQ0,subQ2])],"isStart":false})])]}),makeQuery(id+"F3.opExtrude","SWEPT_FACE",FACE,{"disambiguationData":[OSD([subQ0]),TDD([subQ1])]})],"blendedInto":[makeQuery(id+"F3.opExtrude","SWEPT_FACE",FACE,{"disambiguationData":[OSD([subQ0]),TDD([subQ1])]})]}),makeQuery(id+"F6.opChamfer","BLEND_FACE",FACE,{"disambiguationData":[OSD([subQ0]),TDD([makeQuery(id+"F3.opExtrude","CAP_EDGE",EDGE,{"disambiguationData":[OSD([subQ0]),TDD([subQ1])],"isStart":false})])]})],"blendedInto":[makeQuery(id+"F6.opChamfer","BLEND_FACE",FACE,{"disambiguationData":[OSD([subQ0]),TDD([makeQuery(id+"F3.opExtrude","CAP_EDGE",EDGE,{"disambiguationData":[OSD([subQ0]),TDD([subQ1])],"isStart":false})])]})]});}
            var Q7;
            {var subQ0=sQuery(id+"F0.wireOp",EDGE,"E0.bottom");var subQ1=makeQuery(id+"F1.opExtrude","CAP_EDGE",EDGE,{"disambiguationData":[OSD([subQ0])],"isStart":false});var subQ2=sQuery(id+"F0.wireOp",EDGE,"E0.left");Q7=makeQuery(id+"F15.opChamfer","BLEND_EDGE",EDGE,{"blendedFrom":[makeQuery(id+"F8.opChamfer","BLEND_EDGE",EDGE,{"blendedFrom":[makeQuery(id+"F3.opExtrude","SWEPT_EDGE",EDGE,{"disambiguationData":[OSD([subQ0,subQ2]),TDD([makeQuery(id+"F1.opExtrude","CAP_VERTEX",VERTEX,{"disambiguationData":[OSD([subQ0,subQ2])],"isStart":false})])]}),makeQuery(id+"F3.opExtrude","SWEPT_FACE",FACE,{"disambiguationData":[OSD([subQ0]),TDD([subQ1])]})],"blendedInto":[makeQuery(id+"F3.opExtrude","SWEPT_FACE",FACE,{"disambiguationData":[OSD([subQ0]),TDD([subQ1])]})]}),makeQuery(id+"F6.opChamfer","BLEND_FACE",FACE,{"disambiguationData":[OSD([subQ0]),TDD([makeQuery(id+"F3.opExtrude","CAP_EDGE",EDGE,{"disambiguationData":[OSD([subQ0]),TDD([subQ1])],"isStart":false})])]})],"blendedInto":[makeQuery(id+"F6.opChamfer","BLEND_FACE",FACE,{"disambiguationData":[OSD([subQ0]),TDD([makeQuery(id+"F3.opExtrude","CAP_EDGE",EDGE,{"disambiguationData":[OSD([subQ0]),TDD([subQ1])],"isStart":false})])]})]});}
            var Q8;
            {var subQ0=sQuery(id+"F0.wireOp",EDGE,"E0.left");var subQ1=sQuery(id+"F0.wireOp",EDGE,"E0.bottom");var subQ2=makeQuery(id+"F1.opExtrude","CAP_EDGE",EDGE,{"disambiguationData":[OSD([subQ1])],"isStart":false});Q8=makeQuery(id+"F15.opChamfer","BLEND_EDGE",EDGE,{"blendedFrom":[makeQuery(id+"F8.opChamfer","BLEND_EDGE",EDGE,{"blendedFrom":[makeQuery(id+"F3.opExtrude","SWEPT_EDGE",EDGE,{"disambiguationData":[OSD([subQ1,subQ0]),TDD([makeQuery(id+"F1.opExtrude","CAP_VERTEX",VERTEX,{"disambiguationData":[OSD([subQ1,subQ0])],"isStart":false})])]}),makeQuery(id+"F3.opExtrude","SWEPT_FACE",FACE,{"disambiguationData":[OSD([subQ1]),TDD([subQ2])]})],"blendedInto":[makeQuery(id+"F3.opExtrude","SWEPT_FACE",FACE,{"disambiguationData":[OSD([subQ1]),TDD([subQ2])]})]}),makeQuery(id+"F7.opChamfer","BLEND_FACE",FACE,{"disambiguationData":[OSD([subQ1,subQ0]),TDD([makeQuery(id+"F6.opChamfer","BLEND_EDGE",EDGE,{"blendedFrom":[makeQuery(id+"F3.opExtrude","CAP_EDGE",EDGE,{"disambiguationData":[OSD([subQ1]),TDD([subQ2])],"isStart":false}),makeQuery(id+"F3.opExtrude","SWEPT_FACE",FACE,{"disambiguationData":[OSD([subQ1,subQ0])]})],"blendedInto":[makeQuery(id+"F3.opExtrude","SWEPT_FACE",FACE,{"disambiguationData":[OSD([subQ1,subQ0])]})]})])]})],"blendedInto":[makeQuery(id+"F7.opChamfer","BLEND_FACE",FACE,{"disambiguationData":[OSD([subQ1,subQ0]),TDD([makeQuery(id+"F6.opChamfer","BLEND_EDGE",EDGE,{"blendedFrom":[makeQuery(id+"F3.opExtrude","CAP_EDGE",EDGE,{"disambiguationData":[OSD([subQ1]),TDD([subQ2])],"isStart":false}),makeQuery(id+"F3.opExtrude","SWEPT_FACE",FACE,{"disambiguationData":[OSD([subQ1,subQ0])]})],"blendedInto":[makeQuery(id+"F3.opExtrude","SWEPT_FACE",FACE,{"disambiguationData":[OSD([subQ1,subQ0])]})]})])]})]});}
            var Q9;
            {var subQ0=sQuery(id+"F0.wireOp",EDGE,"E0.left");var subQ1=sQuery(id+"F0.wireOp",EDGE,"E0.bottom");var subQ2=makeQuery(id+"F3.opExtrude","SWEPT_FACE",FACE,{"disambiguationData":[OSD([subQ1,subQ0])]});Q9=makeQuery(id+"F14.opChamfer","BLEND_EDGE",EDGE,{"blendedFrom":[makeQuery(id+"F8.opChamfer","BLEND_EDGE",EDGE,{"blendedFrom":[makeQuery(id+"F3.opExtrude","SWEPT_EDGE",EDGE,{"disambiguationData":[OSD([subQ1,subQ0]),TDD([makeQuery(id+"F1.opExtrude","CAP_VERTEX",VERTEX,{"disambiguationData":[OSD([subQ1,subQ0])],"isStart":true})])]}),subQ2],"blendedInto":[subQ2]}),makeQuery(id+"F7.opChamfer","BLEND_FACE",FACE,{"disambiguationData":[OSD([subQ1,subQ0]),TDD([makeQuery(id+"F6.opChamfer","BLEND_EDGE",EDGE,{"blendedFrom":[makeQuery(id+"F3.opExtrude","CAP_EDGE",EDGE,{"disambiguationData":[OSD([subQ1]),TDD([makeQuery(id+"F1.opExtrude","CAP_EDGE",EDGE,{"disambiguationData":[OSD([subQ1])],"isStart":true})])],"isStart":false}),subQ2],"blendedInto":[subQ2]})])]})],"blendedInto":[makeQuery(id+"F7.opChamfer","BLEND_FACE",FACE,{"disambiguationData":[OSD([subQ1,subQ0]),TDD([makeQuery(id+"F6.opChamfer","BLEND_EDGE",EDGE,{"blendedFrom":[makeQuery(id+"F3.opExtrude","CAP_EDGE",EDGE,{"disambiguationData":[OSD([subQ1]),TDD([makeQuery(id+"F1.opExtrude","CAP_EDGE",EDGE,{"disambiguationData":[OSD([subQ1])],"isStart":true})])],"isStart":false}),subQ2],"blendedInto":[subQ2]})])]})]});}
            var Q10;
            {var subQ0=sQuery(id+"F0.wireOp",EDGE,"E0.left");var subQ1=sQuery(id+"F0.wireOp",EDGE,"E0.bottom");var subQ2=makeQuery(id+"F3.opExtrude","SWEPT_FACE",FACE,{"disambiguationData":[OSD([subQ1,subQ0])]});Q10=makeQuery(id+"F14.opChamfer","BLEND_EDGE",EDGE,{"blendedFrom":[makeQuery(id+"F8.opChamfer","BLEND_EDGE",EDGE,{"blendedFrom":[makeQuery(id+"F3.opExtrude","SWEPT_EDGE",EDGE,{"disambiguationData":[OSD([subQ1,subQ0]),TDD([makeQuery(id+"F1.opExtrude","CAP_VERTEX",VERTEX,{"disambiguationData":[OSD([subQ1,subQ0])],"isStart":false})])]}),subQ2],"blendedInto":[subQ2]}),makeQuery(id+"F7.opChamfer","BLEND_FACE",FACE,{"disambiguationData":[OSD([subQ1,subQ0]),TDD([makeQuery(id+"F6.opChamfer","BLEND_EDGE",EDGE,{"blendedFrom":[makeQuery(id+"F3.opExtrude","CAP_EDGE",EDGE,{"disambiguationData":[OSD([subQ1]),TDD([makeQuery(id+"F1.opExtrude","CAP_EDGE",EDGE,{"disambiguationData":[OSD([subQ1])],"isStart":false})])],"isStart":false}),subQ2],"blendedInto":[subQ2]})])]})],"blendedInto":[makeQuery(id+"F7.opChamfer","BLEND_FACE",FACE,{"disambiguationData":[OSD([subQ1,subQ0]),TDD([makeQuery(id+"F6.opChamfer","BLEND_EDGE",EDGE,{"blendedFrom":[makeQuery(id+"F3.opExtrude","CAP_EDGE",EDGE,{"disambiguationData":[OSD([subQ1]),TDD([makeQuery(id+"F1.opExtrude","CAP_EDGE",EDGE,{"disambiguationData":[OSD([subQ1])],"isStart":false})])],"isStart":false}),subQ2],"blendedInto":[subQ2]})])]})]});}
            var Q11;
            {var subQ0=sQuery(id+"F0.wireOp",EDGE,"E0.bottom");var subQ1=makeQuery(id+"F1.opExtrude","CAP_EDGE",EDGE,{"disambiguationData":[OSD([subQ0])],"isStart":false});Q11=makeQuery(id+"F6.opChamfer","BLEND_EDGE",EDGE,{"blendedFrom":[makeQuery(id+"F3.opExtrude","CAP_EDGE",EDGE,{"disambiguationData":[OSD([subQ0]),TDD([subQ1])],"isStart":false}),makeQuery(id+"F3.opExtrude","SWEPT_FACE",FACE,{"disambiguationData":[OSD([subQ0]),TDD([subQ1])]})],"blendedInto":[makeQuery(id+"F3.opExtrude","SWEPT_FACE",FACE,{"disambiguationData":[OSD([subQ0]),TDD([subQ1])]})]});}
            var Q12;
            {var subQ0=sQuery(id+"F0.wireOp",EDGE,"E0.right");var subQ1=sQuery(id+"F0.wireOp",EDGE,"E0.bottom");var subQ2=makeQuery(id+"F3.opExtrude","SWEPT_FACE",FACE,{"disambiguationData":[OSD([subQ1,subQ0])]});Q12=makeQuery(id+"F14.opChamfer","BLEND_EDGE",EDGE,{"blendedFrom":[makeQuery(id+"F8.opChamfer","BLEND_EDGE",EDGE,{"blendedFrom":[makeQuery(id+"F3.opExtrude","SWEPT_EDGE",EDGE,{"disambiguationData":[OSD([subQ1,subQ0]),TDD([makeQuery(id+"F1.opExtrude","CAP_VERTEX",VERTEX,{"disambiguationData":[OSD([subQ1,subQ0])],"isStart":false})])]}),subQ2],"blendedInto":[subQ2]}),makeQuery(id+"F7.opChamfer","BLEND_FACE",FACE,{"disambiguationData":[OSD([subQ1,subQ0]),TDD([makeQuery(id+"F6.opChamfer","BLEND_EDGE",EDGE,{"blendedFrom":[makeQuery(id+"F3.opExtrude","CAP_EDGE",EDGE,{"disambiguationData":[OSD([subQ1]),TDD([makeQuery(id+"F1.opExtrude","CAP_EDGE",EDGE,{"disambiguationData":[OSD([subQ1])],"isStart":false})])],"isStart":false}),subQ2],"blendedInto":[subQ2]})])]})],"blendedInto":[makeQuery(id+"F7.opChamfer","BLEND_FACE",FACE,{"disambiguationData":[OSD([subQ1,subQ0]),TDD([makeQuery(id+"F6.opChamfer","BLEND_EDGE",EDGE,{"blendedFrom":[makeQuery(id+"F3.opExtrude","CAP_EDGE",EDGE,{"disambiguationData":[OSD([subQ1]),TDD([makeQuery(id+"F1.opExtrude","CAP_EDGE",EDGE,{"disambiguationData":[OSD([subQ1])],"isStart":false})])],"isStart":false}),subQ2],"blendedInto":[subQ2]})])]})]});}
            var Q13;
            {var subQ0=sQuery(id+"F0.wireOp",EDGE,"E0.right");var subQ1=sQuery(id+"F0.wireOp",EDGE,"E0.bottom");var subQ2=makeQuery(id+"F3.opExtrude","SWEPT_FACE",FACE,{"disambiguationData":[OSD([subQ1,subQ0])]});Q13=makeQuery(id+"F14.opChamfer","BLEND_EDGE",EDGE,{"blendedFrom":[makeQuery(id+"F8.opChamfer","BLEND_EDGE",EDGE,{"blendedFrom":[makeQuery(id+"F3.opExtrude","SWEPT_EDGE",EDGE,{"disambiguationData":[OSD([subQ1,subQ0]),TDD([makeQuery(id+"F1.opExtrude","CAP_VERTEX",VERTEX,{"disambiguationData":[OSD([subQ1,subQ0])],"isStart":true})])]}),subQ2],"blendedInto":[subQ2]}),makeQuery(id+"F7.opChamfer","BLEND_FACE",FACE,{"disambiguationData":[OSD([subQ1,subQ0]),TDD([makeQuery(id+"F6.opChamfer","BLEND_EDGE",EDGE,{"blendedFrom":[makeQuery(id+"F3.opExtrude","CAP_EDGE",EDGE,{"disambiguationData":[OSD([subQ1]),TDD([makeQuery(id+"F1.opExtrude","CAP_EDGE",EDGE,{"disambiguationData":[OSD([subQ1])],"isStart":true})])],"isStart":false}),subQ2],"blendedInto":[subQ2]})])]})],"blendedInto":[makeQuery(id+"F7.opChamfer","BLEND_FACE",FACE,{"disambiguationData":[OSD([subQ1,subQ0]),TDD([makeQuery(id+"F6.opChamfer","BLEND_EDGE",EDGE,{"blendedFrom":[makeQuery(id+"F3.opExtrude","CAP_EDGE",EDGE,{"disambiguationData":[OSD([subQ1]),TDD([makeQuery(id+"F1.opExtrude","CAP_EDGE",EDGE,{"disambiguationData":[OSD([subQ1])],"isStart":true})])],"isStart":false}),subQ2],"blendedInto":[subQ2]})])]})]});}
            chamfer(context, id + "F16", {"entities" : qUnion([Q0, Q1, Q2, Q3, Q4, Q5, Q6, Q7, Q8, Q9, Q10, Q11, Q12, Q13]), "width" : 5.08 * mm, "tangentPropagation" : true});
        }
        {
            var Q0;
            {var subQ17=sQuery(id+"F0.wireOp",EDGE,"E0.left");var subQ22=makeQuery(id+"F1.opExtrude","SWEPT_FACE",FACE,{"disambiguationData":[OSD([subQ17])]});var subQ23=sQuery(id+"F9.wireOp",EDGE,"E4");var subQ26=makeQuery(id+"F10.opExtrude","SWEPT_FACE",FACE,{"disambiguationData":[OSD([subQ23])]});var subQ27=makeQuery(id+"F10.boolean.opBoolean","SPLIT",FACE,{"disambiguationData":[TD([subQ22])],"derivedFrom":subQ26});Q0=makeQuery(id+"F12.opChamfer","BLEND_EDGE",EDGE,{"blendedFrom":[makeQuery(id+"F11.opChamfer","BLEND_EDGE",EDGE,{"blendedFrom":[makeQuery(id+"F10.boolean.opBoolean","SPLIT",EDGE,{"disambiguationData":[TD([subQ22])],"derivedFrom":makeQuery(id+"F10.opExtrude","CAP_EDGE",EDGE,{"disambiguationData":[OSD([subQ23])],"isStart":true})}),subQ27],"blendedInto":[subQ27]}),makeQuery(id+"F11.opChamfer","BLEND_EDGE",EDGE,{"blendedFrom":[makeQuery(id+"F10.boolean.opBoolean","SPLIT",EDGE,{"disambiguationData":[TD([subQ22])],"derivedFrom":makeQuery(id+"F10.opExtrude","CAP_EDGE",EDGE,{"disambiguationData":[OSD([subQ23])],"isStart":false})}),subQ27],"blendedInto":[subQ27]})],"blendedInto":[]});}
            var Q1;
            {var subQ14=sQuery(id+"F0.wireOp",EDGE,"E0.right");var subQ20=makeQuery(id+"F1.opExtrude","SWEPT_FACE",FACE,{"disambiguationData":[OSD([subQ14])]});var subQ21=sQuery(id+"F9.wireOp",EDGE,"E4");var subQ26=makeQuery(id+"F10.opExtrude","SWEPT_FACE",FACE,{"disambiguationData":[OSD([subQ21])]});var subQ27=makeQuery(id+"F10.boolean.opBoolean","SPLIT",FACE,{"disambiguationData":[TD([subQ20])],"derivedFrom":subQ26});Q1=makeQuery(id+"F12.opChamfer","BLEND_EDGE",EDGE,{"blendedFrom":[makeQuery(id+"F11.opChamfer","BLEND_EDGE",EDGE,{"blendedFrom":[makeQuery(id+"F10.boolean.opBoolean","SPLIT",EDGE,{"disambiguationData":[TD([subQ20])],"derivedFrom":makeQuery(id+"F10.opExtrude","CAP_EDGE",EDGE,{"disambiguationData":[OSD([subQ21])],"isStart":true})}),subQ27],"blendedInto":[subQ27]}),makeQuery(id+"F11.opChamfer","BLEND_EDGE",EDGE,{"blendedFrom":[makeQuery(id+"F10.boolean.opBoolean","SPLIT",EDGE,{"disambiguationData":[TD([subQ20])],"derivedFrom":makeQuery(id+"F10.opExtrude","CAP_EDGE",EDGE,{"disambiguationData":[OSD([subQ21])],"isStart":false})}),subQ27],"blendedInto":[subQ27]})],"blendedInto":[]});}
            var Q2;
            {var subQ7=sQuery(id+"F0.wireOp",EDGE,"E1.top");var subQ12=sQuery(id+"F9.wireOp",EDGE,"E4");Q2=makeQuery(id+"F10.boolean.opBoolean","SPLIT",FACE,{"disambiguationData":[TD([makeQuery(id+"F1.opExtrude","SWEPT_FACE",FACE,{"disambiguationData":[OSD([subQ7])]})])],"derivedFrom":makeQuery(id+"F10.opExtrude","SWEPT_FACE",FACE,{"disambiguationData":[OSD([subQ12])]})});}
            chamfer(context, id + "F17", {"entities" : qUnion([Q0, Q1, Q2]), "width" : 5.08 * mm, "tangentPropagation" : true});
        }
    });
